# Revit family: gorter_RHTEI1010
name_source: partatom
category: Windows
revit_build: Autodesk Revit 2017 (Build: 20171027_0315(x64)
units: mm (PartAtom-declared; Revit-internal decimal feet)

## family parameters
Always vertical = No
Cut with Voids When Loaded = No
Host = Roof
Room Calculation Point = No
Shared = No

## types (7) — shared parameters
Analytic Construction = <None>
Assembly Code = 37.22.28
Bestendigheid tegen sneeuwbelasting = 405 kg/m²
Bestendigheid tegen windbelasting = 3000 Pa
Brandwerendheid (aantal minuten) = 120 mm  [stored 0.393701 ft]
Constructiesterkte = ± 3000 Pa
Geluidwerendheid = 27 dB
Hard body impact test (EN 356) = Class P5A
Hatch Material = Gorter_Material 1
Isolatiewaarde deksel = Rc = 4,52 (m2.K)W; U = 0,221 W/(m2.K)
Isolatiewaarde opstand = Rc = 4,41 (m2.K)W; U = 0,227 W/(m2.K)
Luchtdichtheid = 0,5 m3/hm1
Manufacturer = Gorter
Model = RHTEI
Oppervlaktebehandeling binnenzijde = Gepoedercoat RAL9010
Gepoedercoat in RAL7011 (buitenzijde) en RAL9010 (binnenzijde).
Gepoedercoat RAL 9010
Oppervlaktebehandeling buitenzijde = Gepoedercoat RAL7011 
Gepoedercoat in RAL7011 (buitenzijde) en RAL9010 (binnenzijde).
Gepoedercoat RAL 7011
Rookdichtheid = R 180
Soft body impact test (EN 13049) = Class 5
URL = http://www.gortergroup.com
Wind- en waterdichtheid = 650 Pa

## per-type parameters (varying)
| type | A | B | Height | Rough Height | Rough Width | Weight (kg) | Width |
| RHTEI7090 | 700 mm  [stored 2.29659 ft] | 900 mm  [stored 2.95276 ft] | 900 mm  [stored 2.95276 ft] | 900 mm  [stored 2.95276 ft] | 700 mm  [stored 2.29659 ft] | 134 | 700 mm  [stored 2.29659 ft] |
| RHTEI9090 | 900 mm  [stored 2.95276 ft] | 900 mm  [stored 2.95276 ft] | 900 mm  [stored 2.95276 ft] | 900 mm  [stored 2.95276 ft] | 900 mm  [stored 2.95276 ft] | 157 | 900 mm  [stored 2.95276 ft] |
| RHTEI7014 | 700 mm  [stored 2.29659 ft] | 1400 mm  [stored 4.59318 ft] | 1400 mm  [stored 4.59318 ft] | 1400 mm  [stored 4.59318 ft] | 700 mm  [stored 2.29659 ft] | 185 | 700 mm  [stored 2.29659 ft] |
| RHTEI1010 | 1000 mm  [stored 3.28084 ft] | 1000 mm  [stored 3.28084 ft] | 1000 mm  [stored 3.28084 ft] | 1000 mm  [stored 3.28084 ft] | 1000 mm  [stored 3.28084 ft] | 180 | 1000 mm  [stored 3.28084 ft] |
| RHTEI1015 | 1000 mm  [stored 3.28084 ft] | 1500 mm  [stored 4.92126 ft] | 1500 mm  [stored 4.92126 ft] | 1500 mm  [stored 4.92126 ft] | 1000 mm  [stored 3.28084 ft] | 236 | 1000 mm  [stored 3.28084 ft] |
| RHTEI1020 | 1000 mm  [stored 3.28084 ft] | 2000 mm  [stored 6.56168 ft] | 2000 mm  [stored 6.56168 ft] | 2000 mm  [stored 6.56168 ft] | 1000 mm  [stored 3.28084 ft] | 298 | 1000 mm  [stored 3.28084 ft] |
| RHTEI9024 | 900 mm  [stored 2.95276 ft] | 2400 mm | 2400 mm | 2400 mm | 900 mm  [stored 2.95276 ft] | 323 | 900 mm  [stored 2.95276 ft] |

note: [stored X ft] marks values corroborated as IEEE doubles in the binary element streams (Revit-internal decimal feet)

## geometry (parser evidence)
native form markers: Sweep x2
no freeform markers — native parametric forms only
